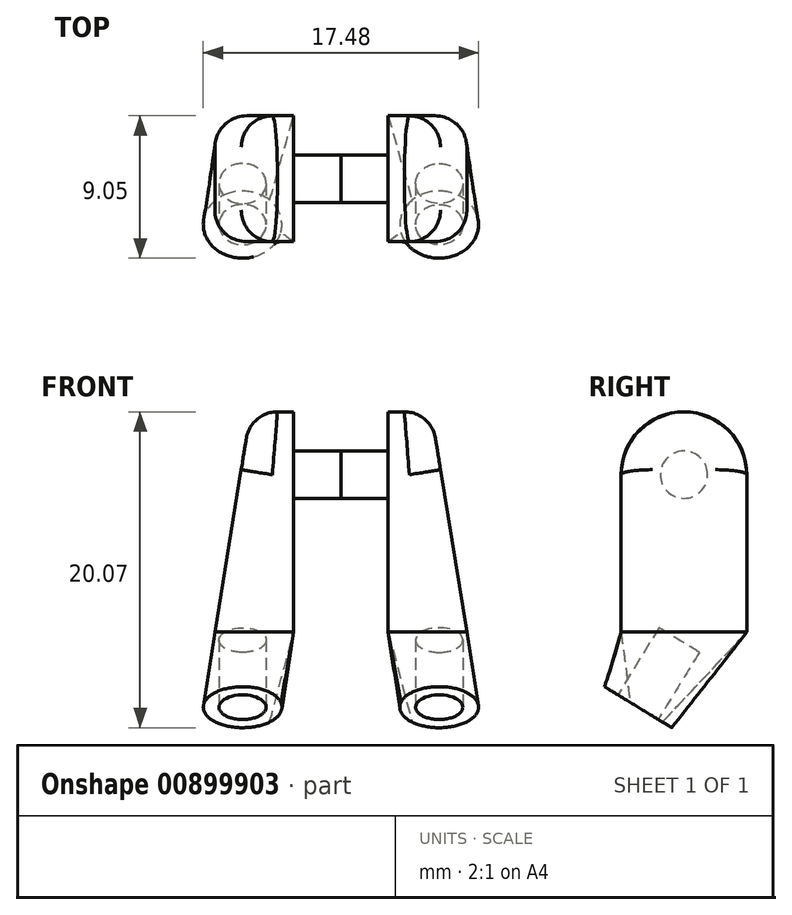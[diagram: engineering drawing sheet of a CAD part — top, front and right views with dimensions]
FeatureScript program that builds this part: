
annotation { "Feature Type Name" : "Feature", "Feature Type Description" : "" }
export const myFeature = defineFeature(function(context is Context, id is Id, definition is map)
    precondition{}
    {
        {
            var Q0;
            Q0=qCreatedBy(makeId("Right.planeOp"),FACE);
            var sketch = newSketch(context, id + "F0", { "sketchPlane" : qUnion([Q0])});
            skCircle(sketch, "E0", {"center": v(0, 0) * mm, "radius": 1.5 * mm});
            skSolve(sketch);
        }
        {
            var Q0;
            Q0 = qSketchRegion(id + "F0", true);
            extrude(context, id + "F1", {"entities" : qUnion([Q0]), "depth" : 3 * mm, "offsetDistance" : 25.4 * mm});
        }
        {
            var Q0;
            Q0=makeQuery(id+"F1.opExtrude","CAP_FACE",FACE,{"disambiguationData":[OSD([sQuery(id+"F0.wireOp",EDGE,"E0")])],"isStart":false});
            var sketch = newSketch(context, id + "F2", { "sketchPlane" : qUnion([Q0])});
            skArc(sketch, "E1", {"start": v(4, 0) * mm, "mid": v(0, 4) * mm, "end": v(-4, 0) * mm});
            skLineSegment(sketch, "E2.top", {"start": v(4, -10) * mm, "end": v(-4, -10) * mm});
            skLineSegment(sketch, "E2.left", {"start": v(4, 0) * mm, "end": v(4, -10) * mm});
            skLineSegment(sketch, "E2.right", {"start": v(-4, 0) * mm, "end": v(-4, -10) * mm});
            skPoint(sketch, "E2.middle", {"position": v(0, -5) * mm});
            skLineSegment(sketch, "E3", {"start": v(-5.82, -12.99) * mm, "end": v(-4, -10) * mm, "construction": true});
            skPoint(sketch, "E4.start.orphan", {"position": v(0, -16.55) * mm});
            skLineSegment(sketch, "E5", {"start": v(4, -10) * mm, "end": v(0, -16.55) * mm, "construction": true});
            skLineSegment(sketch, "E6", {"start": v(0, -16.55) * mm, "end": v(-5.82, -12.99) * mm, "construction": true});
            skLineSegment(sketch, "E7", {"start": v(-2.91, -14.77) * mm, "end": v(-1.83, -13) * mm});
            skSolve(sketch);
        }
        {
            var Q0;
            Q0 = qSketchRegion(id + "F2", true);
            extrude(context, id + "F3", {"entities" : qUnion([Q0]), "operationType" : NewBodyOperationType.ADD, "depth" : 5 * mm, "offsetDistance" : 25.4 * mm});
        }
        {
            var Q0;
            Q0=makeQuery(id+"F3.opExtrude","SWEPT_FACE",FACE,{"disambiguationData":[OSD([sQuery(id+"F2.wireOp",EDGE,"E2.right")])]});
            var sketch = newSketch(context, id + "F4", { "sketchPlane" : qUnion([Q0])});
            skLineSegment(sketch, "E8", {"start": v(8, -10) * mm, "end": v(5.5, 5.42) * mm});
            skPoint(sketch, "E8.endSnap0", {"position": v(5.5, 0) * mm});
            skLineSegment(sketch, "E9", {"start": v(5.5, 5.42) * mm, "end": v(11.1, 5.42) * mm});
            skLineSegment(sketch, "E10", {"start": v(11.1, 5.42) * mm, "end": v(8, -10) * mm});
            skSolve(sketch);
        }
        {
            var Q0;
            Q0 = qSketchRegion(id + "F4", true);
            extrude(context, id + "F5", {"entities" : qUnion([Q0]), "operationType" : NewBodyOperationType.REMOVE, "oppositeDirection" : true, "depth" : 25.4 * mm, "offsetDistance" : 25.4 * mm});
        }
        {
            var Q0;
            Q0=makeQuery(id+"F5.boolean.opBoolean","COPY",EDGE,{"derivedFrom":makeQuery(id+"F5.opExtrude","CAP_EDGE",EDGE,{"disambiguationData":[OSD([sQuery(id+"F4.wireOp",EDGE,"E8")])],"isStart":true})});
            var Q1;
            Q1=makeQuery(id+"F5.boolean.opBoolean","INTERSECT",EDGE,{"derivedFrom":[makeQuery(id+"F3.opExtrude","SWEPT_FACE",FACE,{"disambiguationData":[OSD([sQuery(id+"F2.wireOp",EDGE,"E1")])]}),makeQuery(id+"F5.opExtrude","SWEPT_FACE",FACE,{"disambiguationData":[OSD([sQuery(id+"F4.wireOp",EDGE,"E8")])]})]});
            var Q2;
            Q2=makeQuery(id+"F5.boolean.opBoolean","INTERSECT",EDGE,{"derivedFrom":[makeQuery(id+"F3.opExtrude","SWEPT_FACE",FACE,{"disambiguationData":[OSD([sQuery(id+"F2.wireOp",EDGE,"E2.left")])]}),makeQuery(id+"F5.opExtrude","SWEPT_FACE",FACE,{"disambiguationData":[OSD([sQuery(id+"F4.wireOp",EDGE,"E8")])]})]});
            fillet(context, id + "F6", {"entities" : qUnion([Q0, Q1, Q2]), "radius" : 2 * mm, "tangentPropagation" : true, "allowEdgeOverflow" : false});
        }
        {
            var Q0;
            Q0=sQuery(id+"F2.wireOp",VERTEX,"E3.start");
            var Q1;
            Q1=sQuery(id+"F2.wireOp",EDGE,"E3");
            cPlane(context, id + "F7", {"entities" : qUnion([Q0, Q1]), "cplaneType" : CPlaneType.LINE_POINT, "offset" : 25.4 * mm, "width" : 152.4 * mm, "height" : 152.4 * mm});
        }
        {
            var Q0;
            Q0=qCreatedBy(id+"F7.planeOp",FACE);
            var sketch = newSketch(context, id + "F8", { "sketchPlane" : qUnion([Q0])});
            skLineSegment(sketch, "E11", {"start": v(3, 5.21) * mm, "end": v(13.69, 5.21) * mm, "construction": true});
            skCircle(sketch, "E12", {"center": v(6.24, 5.21) * mm, "radius": 2.5 * mm});
            skSolve(sketch);
        }
        {
            var Q1;
            Q1=makeQuery(id+"F3.opExtrude","SWEPT_FACE",FACE,{"disambiguationData":[OSD([sQuery(id+"F2.wireOp",EDGE,"E2.top")])]});
            var Q2;
            Q2=makeQuery(id+"F8.imprint","IMPRINT",FACE,{"disambiguationData":[TD([[makeQuery(id+"F8.imprint","IMPRINT",EDGE,{"derivedFrom":sQuery(id+"F8.wireOp",EDGE,"E12")}),1.0]])]});
            loft(context, id + "F9", {"operationType" : NewBodyOperationType.ADD, "sheetProfilesArray" : [{ "sheetProfileEntities" : qUnion([Q1]) }, { "sheetProfileEntities" : qUnion([Q2]) }]});
        }
        {
            var Q0;
            Q0=makeQuery(id+"F9.opLoft","CAP_FACE",FACE,{"disambiguationData":[OSD([makeQuery(id+"F8.imprint","IMPRINT",FACE,{"disambiguationData":[TD([[makeQuery(id+"F8.imprint","IMPRINT",EDGE,{"derivedFrom":sQuery(id+"F8.wireOp",EDGE,"E12")}),1.0]])]})])],"isStart":true});
            var sketch = newSketch(context, id + "F10", { "sketchPlane" : qUnion([Q0])});
            skCircle(sketch, "E13", {"center": v(6.24, -5.21) * mm, "radius": 1.5 * mm});
            skSolve(sketch);
        }
        {
            var Q0;
            Q0 = qSketchRegion(id + "F10", true);
            extrude(context, id + "F11", {"entities" : qUnion([Q0]), "operationType" : NewBodyOperationType.REMOVE, "oppositeDirection" : true, "depth" : 5 * mm, "offsetDistance" : 25.4 * mm});
        }
        {
            var Q0;
            Q0=makeQuery(id+"F1.opExtrude","SWEPT_BODY",BODY,{"disambiguationData":[OSD([sQuery(id+"F0.wireOp",EDGE,"E0")])]});
            var Q1;
            Q1=makeQuery(id+"F1.opExtrude","CAP_FACE",FACE,{"disambiguationData":[OSD([sQuery(id+"F0.wireOp",EDGE,"E0")])],"isStart":true});
            mirror(context, id + "F12", {"entities" : qUnion([Q0]), "mirrorPlane" : qUnion([Q1])});
        }
    });
